# Revit family: Electronics_Commercial-Loudspeakers_Biamp_Two-Way-Edge-Loudspeaker_CM20DT
name_source: partatom
category: Communication Devices
units: mm (PartAtom-declared; Revit-internal decimal feet)

## family parameters
Cut with Voids When Loaded = No
Host = Face
Maintain Annotation Orientation = No
OmniClass Number = 23.85.10.11.14.14.14
OmniClass Title = Loudspeakers
Part Type = Normal
Room Calculation Point = No
Round Connector Dimension = Use Diameter
Shared = No

## types (1)
- CM20DT
    100V transformer power taps in watts = 20 - 10 - 5
    70V transformer power taps in = 20 - 10 - 5 - 2.5
    Applicable low impedance = Yes
    Closest RAL colour (subject to deviations) = RAL9010
    Colour = White
    Connector Description = Terminal strip; 70V/100V operation
    Cutout in mm = 186
    Default Elevation = 48 "
    Depth = 3 "
    Description = CM20DT 6.5 Two-Way, Thin Edge Ceiling Loudspeaker, White
    Diameter = 8 "
    Frequency response in Hz = 60 - 20K
    Grille main material = Steel
    Housing Material = Biamp - Plastic - White
    IP rating = 50
    Impedance in ohms = 16
    Installation grip range in mm = 2 - 25
    Loudspeaker system = 2-way
    Low impedance RMS power in watts = 30
    Low impedance dynamic power in watts = 60
    Main construction material = ABS plastic
    Manufacturer = Biamp
    Max SPL 1m in dB = 104
    Model = CM20DT
    Mounting system = 3 screws
    Product Documentation Link = https://downloads.biamp.com
    Product Page URL = https://www.biamp.com
    Product data url = https://bimobject.com
    SPL 1W/1m in dB = 86
    Tweeter size in inch = 1
    URL = https://www.biamp.com
    Version = 1
    Vertical dispersion angle 1000 Hz = 180°
    Weight = 2.73 lb
    Woofer cone material = Polypropylene
    Woofer size in inch = 6.5

## geometry (parser evidence)
native form markers: Sweep x2
no freeform markers — native parametric forms only
